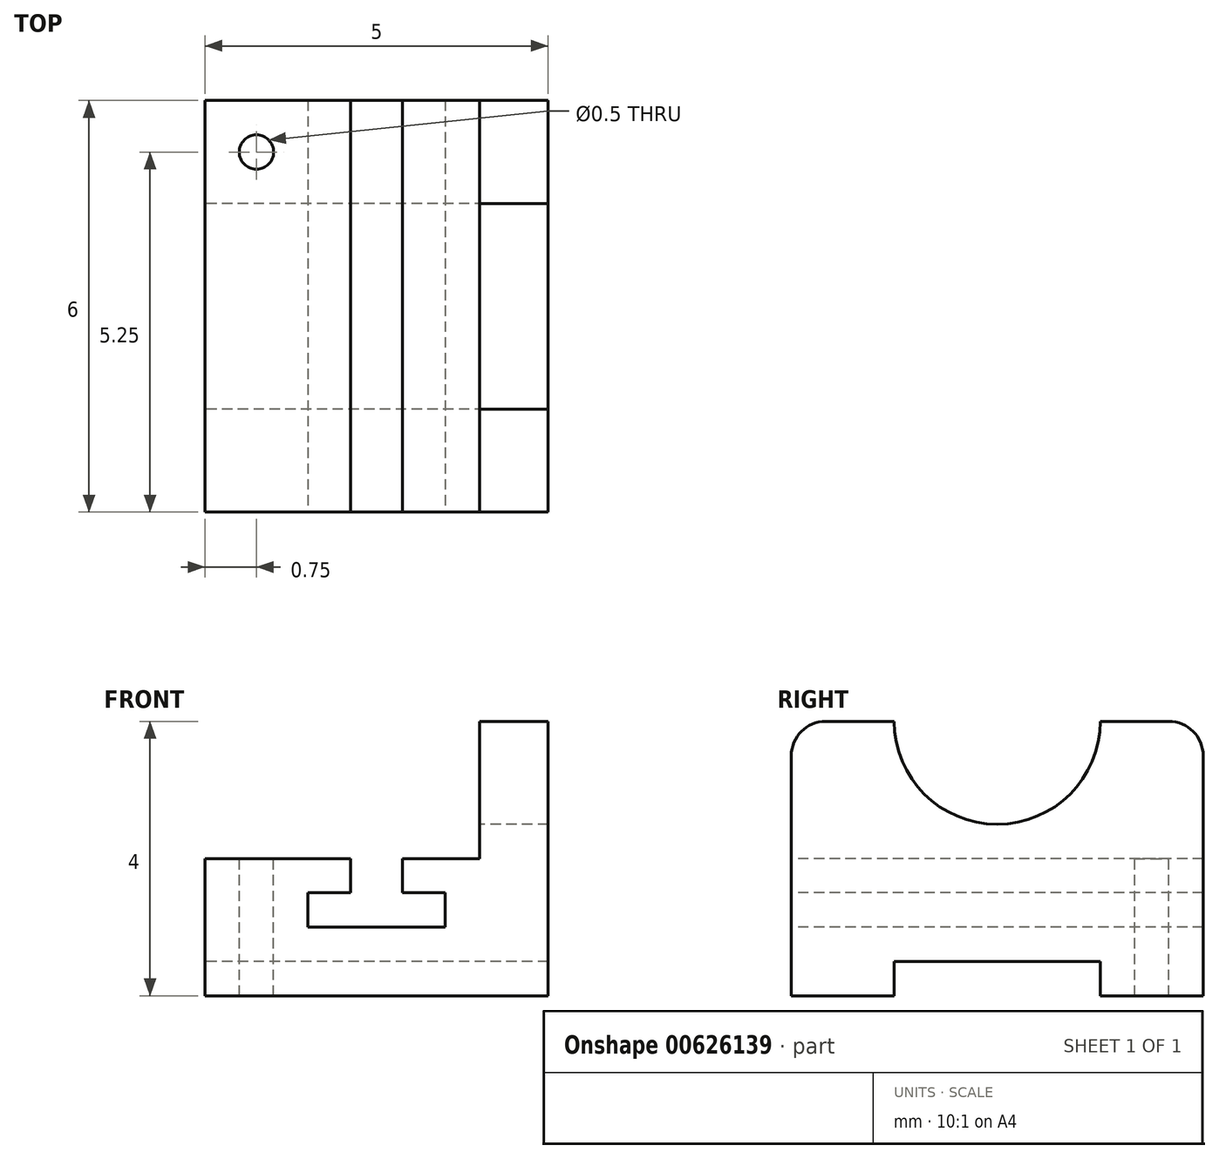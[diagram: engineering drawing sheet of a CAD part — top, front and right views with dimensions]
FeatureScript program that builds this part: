
annotation { "Feature Type Name" : "Feature", "Feature Type Description" : "" }
export const myFeature = defineFeature(function(context is Context, id is Id, definition is map)
    precondition{}
    {
        {
            var Q0;
            Q0=qCreatedBy(makeId("Front.planeOp"),FACE);
            var sketch = newSketch(context, id + "F0", { "sketchPlane" : qUnion([Q0])});
            skLineSegment(sketch, "E0.bottom", {"start": v(2.5, 2) * mm, "end": v(-2.5, 2) * mm});
            skLineSegment(sketch, "E0.top", {"start": v(2.5, -2) * mm, "end": v(-2.5, -2) * mm});
            skLineSegment(sketch, "E0.left", {"start": v(2.5, 2) * mm, "end": v(2.5, -2) * mm});
            skLineSegment(sketch, "E0.right", {"start": v(-2.5, 2) * mm, "end": v(-2.5, -2) * mm});
            skPoint(sketch, "E0.middle", {"position": v(0, 0) * mm});
            skSolve(sketch);
        }
        {
            var Q0;
            Q0=makeQuery(id+"F0.imprint","IMPRINT",FACE,{"disambiguationData":[TD([[makeQuery(id+"F0.imprint","IMPRINT",EDGE,{"derivedFrom":sQuery(id+"F0.wireOp",EDGE,"E0.bottom")}),1.0]])]});
            extrude(context, id + "F1", {"entities" : qUnion([Q0]), "depth" : 6 * mm, "offsetDistance" : 25 * mm});
        }
        {
            var Q0;
            Q0=makeQuery(id+"F1.opExtrude","CAP_FACE",FACE,{"disambiguationData":[OSD([sQuery(id+"F0.wireOp",EDGE,"E0.bottom"),sQuery(id+"F0.wireOp",EDGE,"E0.top"),sQuery(id+"F0.wireOp",EDGE,"E0.left"),sQuery(id+"F0.wireOp",EDGE,"E0.right")])],"isStart":false});
            var sketch = newSketch(context, id + "F2", { "sketchPlane" : qUnion([Q0])});
            skLineSegment(sketch, "E1.bottom", {"start": v(-2.5, 2) * mm, "end": v(1.5, 2) * mm});
            skLineSegment(sketch, "E1.top", {"start": v(-2.5, 0) * mm, "end": v(1.5, 0) * mm});
            skLineSegment(sketch, "E1.left", {"start": v(-2.5, 2) * mm, "end": v(-2.5, 0) * mm});
            skLineSegment(sketch, "E1.right", {"start": v(1.5, 2) * mm, "end": v(1.5, 0) * mm});
            skSolve(sketch);
        }
        {
            var Q0;
            Q0 = qSketchRegion(id + "F2", true);
            extrude(context, id + "F3", {"entities" : qUnion([Q0]), "operationType" : NewBodyOperationType.REMOVE, "endBound" : BoundingType.THROUGH_ALL, "oppositeDirection" : true, "depth" : 25 * mm, "offsetDistance" : 25 * mm});
        }
        {
            var Q0;
            Q0=makeQuery(id+"F1.opExtrude","CAP_FACE",FACE,{"disambiguationData":[OSD([sQuery(id+"F0.wireOp",EDGE,"E0.bottom"),sQuery(id+"F0.wireOp",EDGE,"E0.top"),sQuery(id+"F0.wireOp",EDGE,"E0.left"),sQuery(id+"F0.wireOp",EDGE,"E0.right")])],"isStart":false});
            var sketch = newSketch(context, id + "F4", { "sketchPlane" : qUnion([Q0])});
            skLineSegment(sketch, "E2", {"start": v(0.37, 0) * mm, "end": v(0.37, -0.5) * mm});
            skLineSegment(sketch, "E3", {"start": v(0.37, -0.5) * mm, "end": v(-1, -0.5) * mm});
            skLineSegment(sketch, "E4", {"start": v(-1, -0.5) * mm, "end": v(-1, -1) * mm});
            skLineSegment(sketch, "E5", {"start": v(-1, -1) * mm, "end": v(1, -1) * mm});
            skLineSegment(sketch, "E6", {"start": v(1, -1) * mm, "end": v(1, -0.5) * mm});
            skLineSegment(sketch, "E7", {"start": v(1, -0.5) * mm, "end": v(-0.38, -0.5) * mm});
            skLineSegment(sketch, "E8", {"start": v(-0.38, -0.5) * mm, "end": v(-0.38, 0) * mm});
            skSolve(sketch);
        }
        {
            var Q0;
            {var subQ0=sQuery(id+"F4.wireOp",EDGE,"E2");Q0=makeQuery(id+"F4.imprint","IMPRINT",FACE,{"disambiguationData":[TD([[makeQuery(id+"F4.imprint","IMPRINT",EDGE,{"derivedFrom":subQ0}),-1.0]])]});}
            var Q1;
            {var subQ1=sQuery(id+"F4.wireOp",EDGE,"E3");Q1=makeQuery(id+"F4.imprint","IMPRINT",FACE,{"disambiguationData":[TD([[makeQuery(id+"F4.imprint","IMPRINT",EDGE,{"derivedFrom":subQ1}),1.0]])]});}
            extrude(context, id + "F5", {"entities" : qUnion([Q0, Q1]), "operationType" : NewBodyOperationType.REMOVE, "endBound" : BoundingType.THROUGH_ALL, "oppositeDirection" : true, "depth" : 25 * mm, "offsetDistance" : 25 * mm});
        }
        {
            var Q0;
            Q0=makeQuery(id+"F1.opExtrude","SWEPT_FACE",FACE,{"disambiguationData":[OSD([sQuery(id+"F0.wireOp",EDGE,"E0.right")])]});
            var sketch = newSketch(context, id + "F6", { "sketchPlane" : qUnion([Q0])});
            skLineSegment(sketch, "E9.bottom", {"start": v(1.5, -2) * mm, "end": v(4.5, -2) * mm});
            skLineSegment(sketch, "E9.top", {"start": v(1.5, -1.5) * mm, "end": v(4.5, -1.5) * mm});
            skLineSegment(sketch, "E9.left", {"start": v(1.5, -2) * mm, "end": v(1.5, -1.5) * mm});
            skLineSegment(sketch, "E9.right", {"start": v(4.5, -2) * mm, "end": v(4.5, -1.5) * mm});
            skSolve(sketch);
        }
        {
            var Q0;
            Q0=makeQuery(id+"F6.imprint","IMPRINT",FACE,{"disambiguationData":[TD([[makeQuery(id+"F6.imprint","IMPRINT",EDGE,{"derivedFrom":sQuery(id+"F6.wireOp",EDGE,"E9.bottom")}),-1.0]])]});
            extrude(context, id + "F7", {"entities" : qUnion([Q0]), "operationType" : NewBodyOperationType.REMOVE, "endBound" : BoundingType.THROUGH_ALL, "oppositeDirection" : true, "depth" : 25 * mm, "offsetDistance" : 25 * mm});
        }
        {
            var Q0;
            Q0=makeQuery(id+"F3.boolean.opBoolean","COPY",FACE,{"derivedFrom":makeQuery(id+"F3.opExtrude","SWEPT_FACE",FACE,{"disambiguationData":[OSD([sQuery(id+"F2.wireOp",EDGE,"E1.right")])]})});
            var sketch = newSketch(context, id + "F8", { "sketchPlane" : qUnion([Q0])});
            skCircle(sketch, "E10", {"center": v(3, 2) * mm, "radius": 1.5 * mm});
            skSolve(sketch);
        }
        {
            var Q0;
            Q0 = qSketchRegion(id + "F8", true);
            extrude(context, id + "F9", {"entities" : qUnion([Q0]), "operationType" : NewBodyOperationType.REMOVE, "endBound" : BoundingType.THROUGH_ALL, "oppositeDirection" : true, "depth" : 25 * mm, "offsetDistance" : 25 * mm});
        }
        {
            var Q0;
            Q0=makeQuery(id+"F1.opExtrude","CAP_EDGE",EDGE,{"disambiguationData":[OSD([sQuery(id+"F0.wireOp",EDGE,"E0.bottom")])],"isStart":false});
            var Q1;
            Q1=makeQuery(id+"F1.opExtrude","CAP_EDGE",EDGE,{"disambiguationData":[OSD([sQuery(id+"F0.wireOp",EDGE,"E0.bottom")])],"isStart":true});
            fillet(context, id + "F10", {"entities" : qUnion([Q0, Q1]), "radius" : 0.5 * mm, "tangentPropagation" : true, "allowEdgeOverflow" : false});
        }
        {
            var Q0;
            {var subQ0=sQuery(id+"F0.wireOp",EDGE,"E0.right");Q0=makeQuery(id+"F5.boolean.opBoolean","SPLIT",FACE,{"disambiguationData":[TD([makeQuery(id+"F1.opExtrude","SWEPT_FACE",FACE,{"disambiguationData":[OSD([subQ0])]})])],"derivedFrom":makeQuery(id+"F3.boolean.opBoolean","COPY",FACE,{"derivedFrom":makeQuery(id+"F3.opExtrude","SWEPT_FACE",FACE,{"disambiguationData":[OSD([sQuery(id+"F2.wireOp",EDGE,"E1.top")])]})})});}
            var sketch = newSketch(context, id + "F11", { "sketchPlane" : qUnion([Q0])});
            skCircle(sketch, "E11", {"center": v(-1.75, -0.75) * mm, "radius": 0.25 * mm});
            skLineSegment(sketch, "E12", {"start": v(-0.38, -3) * mm, "end": v(-2.5, -3) * mm, "construction": true});
            skSolve(sketch);
        }
        {
            var Q0;
            Q0 = qSketchRegion(id + "F11", true);
            extrude(context, id + "F12", {"entities" : qUnion([Q0]), "operationType" : NewBodyOperationType.REMOVE, "endBound" : BoundingType.THROUGH_ALL, "oppositeDirection" : true, "depth" : 25 * mm, "offsetDistance" : 25 * mm});
        }
        {
            var Q0;
            Q0=makeQuery(id+"F1.opExtrude","CAP_FACE",FACE,{"disambiguationData":[OSD([sQuery(id+"F0.wireOp",EDGE,"E0.bottom"),sQuery(id+"F0.wireOp",EDGE,"E0.top"),sQuery(id+"F0.wireOp",EDGE,"E0.left"),sQuery(id+"F0.wireOp",EDGE,"E0.right")])],"isStart":true});
            cPlane(context, id + "F13", {"entities" : qUnion([Q0]), "cplaneType" : CPlaneType.OFFSET, "offset" : 3 * mm, "oppositeDirection" : true, "width" : 150 * mm, "height" : 150 * mm});
        }
    });
